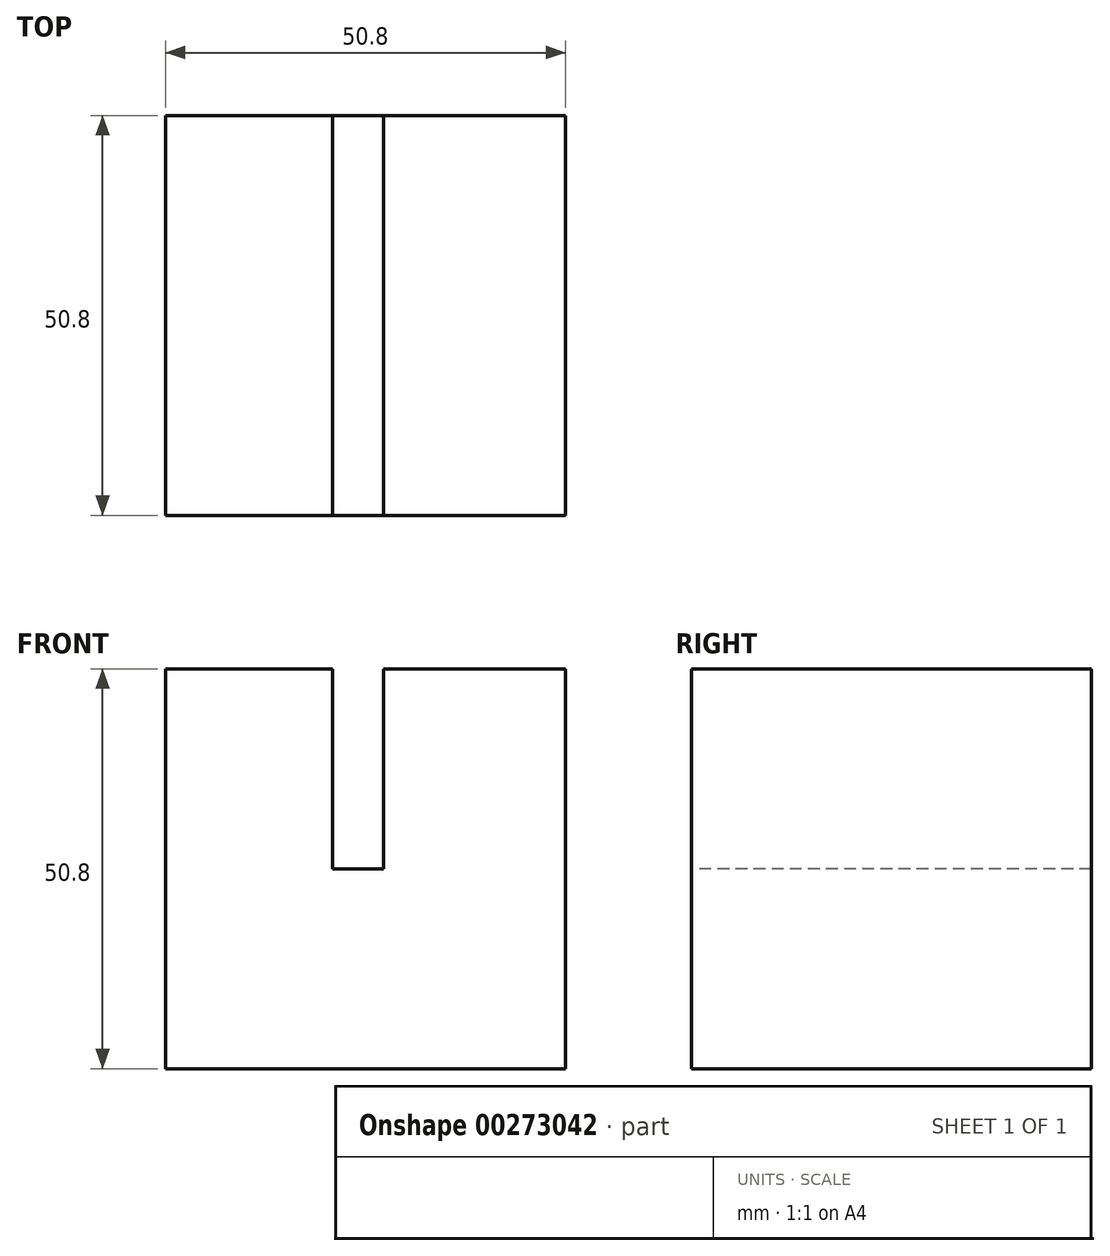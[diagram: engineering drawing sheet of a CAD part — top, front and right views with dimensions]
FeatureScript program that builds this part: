
annotation { "Feature Type Name" : "Feature", "Feature Type Description" : "" }
export const myFeature = defineFeature(function(context is Context, id is Id, definition is map)
    precondition{}
    {
        {
            var Q0;
            Q0=qCreatedBy(makeId("Front.planeOp"),FACE);
            var sketch = newSketch(context, id + "F0", { "sketchPlane" : qUnion([Q0])});
            skLineSegment(sketch, "E0.bottom", {"start": v(0, 0) * mm, "end": v(-50.8, 0) * mm});
            skLineSegment(sketch, "E0.top", {"start": v(0, 50.8) * mm, "end": v(-50.8, 50.8) * mm});
            skLineSegment(sketch, "E0.left", {"start": v(0, 0) * mm, "end": v(0, 50.8) * mm});
            skLineSegment(sketch, "E0.right", {"start": v(-50.8, 0) * mm, "end": v(-50.8, 50.8) * mm});
            skSolve(sketch);
        }
        {
            var Q0;
            Q0 = qSketchRegion(id + "F0", true);
            extrude(context, id + "F1", {"entities" : qUnion([Q0]), "depth" : 50.8 * mm});
        }
        {
            var Q0;
            Q0=makeQuery(id+"F1.opExtrude","SWEPT_FACE",FACE,{"disambiguationData":[OSD([sQuery(id+"F0.wireOp",EDGE,"E0.top")])]});
            var sketch = newSketch(context, id + "F2", { "sketchPlane" : qUnion([Q0])});
            skLineSegment(sketch, "E1.bottom", {"start": v(-29.6, 0) * mm, "end": v(-23.1, 0) * mm});
            skLineSegment(sketch, "E1.top", {"start": v(-29.6, -50.8) * mm, "end": v(-23.1, -50.8) * mm});
            skLineSegment(sketch, "E1.left", {"start": v(-29.6, 0) * mm, "end": v(-29.6, -50.8) * mm});
            skLineSegment(sketch, "E1.right", {"start": v(-23.1, 0) * mm, "end": v(-23.1, -50.8) * mm});
            skPoint(sketch, "E1.middle", {"position": v(-26.35, -25.4) * mm});
            skSolve(sketch);
        }
        {
            var Q0;
            Q0=makeQuery(id+"F2.imprint","IMPRINT",FACE,{"disambiguationData":[TD([[makeQuery(id+"F2.imprint","IMPRINT",EDGE,{"derivedFrom":sQuery(id+"F2.wireOp",EDGE,"E1.bottom")}),1.0]])]});
            extrude(context, id + "F3", {"entities" : qUnion([Q0]), "operationType" : NewBodyOperationType.REMOVE, "oppositeDirection" : true, "depth" : 25.4 * mm});
        }
    });
